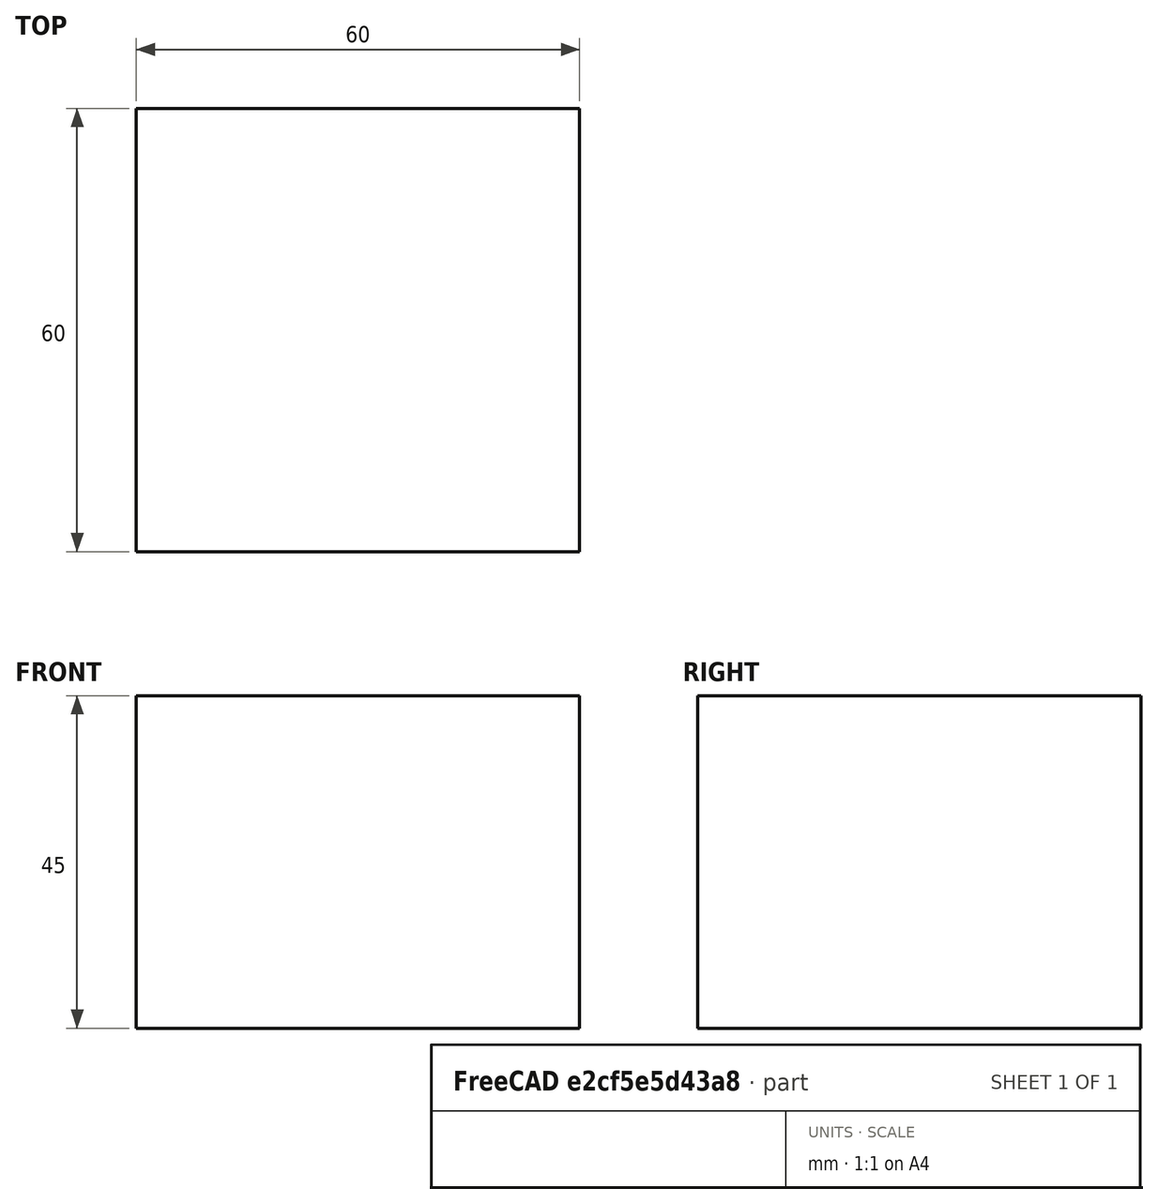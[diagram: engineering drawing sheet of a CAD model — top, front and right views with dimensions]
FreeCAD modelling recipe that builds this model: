
FCSTD DOCUMENT  (FreeCAD 0.15R4671 (Git))
Label: cad2
License: All rights reserved
LicenseURL: http://en.wikipedia.org/wiki/All_rights_reserved
objects: Part::Box×1, Sketcher::SketchObject×1
note: 2 computed .brp shape members not serialized (recipe doc carries the construction recipe); baked Part::Feature solids carry a one-line shape summary decoded from their .brp

FEATURE [Part::Box] Box  label="Cubo"
  Height = 45
  Length = 60
  Width = 60
FEATURE [Sketcher::SketchObject] Sketch
  Placement = pos=(0,0,45) rot=(0,0,1;0rad)
  sketch-geometry (27):
    g0: LineSegment StartX=5 StartY=55 StartZ=0 EndX=55 EndY=55 EndZ=0
    g1: LineSegment StartX=5 StartY=5 StartZ=0 EndX=55 EndY=5 EndZ=0
    g2: LineSegment StartX=5 StartY=55 StartZ=0 EndX=5 EndY=37.5 EndZ=0
    g3: LineSegment StartX=5 StartY=5 StartZ=0 EndX=5 EndY=22.5 EndZ=0
    g4: LineSegment StartX=5 StartY=22.5 StartZ=0 EndX=10 EndY=22.5 EndZ=0
    g5: LineSegment StartX=10 StartY=37.5 StartZ=0 EndX=5.0106 EndY=37.5 EndZ=0
    g6: LineSegment StartX=55 StartY=55 StartZ=0 EndX=55 EndY=37.5 EndZ=0
    g7: LineSegment StartX=55 StartY=5 StartZ=0 EndX=55 EndY=22.5 EndZ=0
    g8: LineSegment StartX=55 StartY=37.5 StartZ=0 EndX=50 EndY=37.5 EndZ=0
    g9: LineSegment StartX=50 StartY=22.5 StartZ=0 EndX=55 EndY=22.5 EndZ=0
    g10: GeomPoint [constr] X=60 Y=0 Z=0
    g11: GeomPoint [constr] X=60 Y=60 Z=0
    g12: GeomPoint [constr] X=0 Y=60 Z=0
    g13: LineSegment StartX=50.001 StartY=37.5 StartZ=0 EndX=45 EndY=37.5 EndZ=0
    g14: LineSegment StartX=45 StartY=37.5 StartZ=0 EndX=45 EndY=32.5 EndZ=0
    g15: LineSegment StartX=45 StartY=32.5 StartZ=0 EndX=50 EndY=32.5 EndZ=0
    g16: LineSegment StartX=50 StartY=27.5 StartZ=0 EndX=45 EndY=27.5 EndZ=0
    g17: LineSegment StartX=45 StartY=27.5 StartZ=0 EndX=45 EndY=22.5 EndZ=0
    g18: LineSegment StartX=45 StartY=22.5 StartZ=0 EndX=50.0094 EndY=22.4998 EndZ=0
    g19: LineSegment StartX=50 StartY=32.5 StartZ=0 EndX=50 EndY=27.5 EndZ=0
    g20: LineSegment StartX=10 StartY=37.5 StartZ=0 EndX=15 EndY=37.5 EndZ=0
    g21: LineSegment StartX=15 StartY=37.5 StartZ=0 EndX=15 EndY=32.5 EndZ=0
    g22: LineSegment StartX=15 StartY=32.5 StartZ=0 EndX=10 EndY=32.5 EndZ=0
    g23: LineSegment StartX=10 StartY=32.4939 StartZ=0 EndX=10 EndY=27.5 EndZ=0
    g24: LineSegment StartX=10 StartY=27.5 StartZ=0 EndX=15 EndY=27.5 EndZ=0
    g25: LineSegment StartX=15 StartY=27.5 StartZ=0 EndX=15 EndY=22.5 EndZ=0
    g26: LineSegment StartX=15 StartY=22.5 StartZ=0 EndX=10 EndY=22.5 EndZ=0
  constraints (80):
    c: DistanceY(g2,g0) = 17.5
    c: DistanceY(g5,g0) = 17.5
    c: DistanceX(g5,g2) = -5
    c: DistanceX(g4,g3) = -5
    c: DistanceY(g3,g1) = -17.5
    c: DistanceY(g2,g1) = -50
    c: DistanceY(g3,g0) = 50
    c: DistanceX(g1,g1) = 50
    c: DistanceY(g-1,g1) = 5
    c: DistanceX(g-1,g3) = 5
    c: DistanceY(g-1,g1) = 5
    c: DistanceY(g-1,g7) = 5
    c: DistanceY(g1,g0) = 50
    c: DistanceY(g1,g6) = 50
    c: DistanceX(g6,g8) = -5
    c: DistanceX(g9,g7) = 5
    c: DistanceY(g7,g1) = -17.5
    c: DistanceY(g8,g0) = 17.5
    c: DistanceX(g0,g0) = 50
    c: DistanceX(g1,g7) = 50
    c: DistanceX(g-1,g1) = 5
    c: DistanceX(g-1,g0) = 5
    c: DistanceX(g1,g10) = 5
    c: DistanceY(g1,g10) = -5
    c: DistanceX(g0,g11) = 5
    c: DistanceX(g6,g11) = 5
    c: DistanceY(g0,g11) = 5
    c: DistanceX(g8,g11) = 5
    c: DistanceX(g9,g11) = 10
    c: DistanceX(g9,g10) = 5
    c: DistanceX(g6,g11) = 5
    c: DistanceX(g8,g5) = -40
    c: DistanceX(g12,g2) = 5
    c: DistanceX(g12,g0) = 5
    c: DistanceY(g12,g0) = -5
    c: Coincident(g13,g14)
    c: Coincident(g14,g15)
    c: DistanceY(g13,g15) = -5
    c: DistanceY(g13,g14) = -5
    c: DistanceY(g8,g14) = -5
    c: DistanceY(g15,g8) = 5
    c: DistanceX(g6,g14) = -10
    c: Coincident(g16,g17)
    c: Coincident(g17,g18)
    c: DistanceX(g16,g16) = 5
    c: DistanceY(g16,g17) = -5
    c: DistanceY(g16,g9) = -5
    c: DistanceX(g15,g14) = -5
    c: DistanceX(g19,g16) = -5
    c: DistanceY(g19,g15) = 5
    c: DistanceY(g16,g15) = 5
    c: DistanceY(g19,g16) = -5
    c: DistanceY(g19,g16) = -5
    c: DistanceX(g16,g19) = 5
    c: DistanceX(g17,g7) = 10
    c: DistanceY(g7,g16) = 5
    c: Coincident(g20,g21)
    c: Coincident(g21,g22)
    c: Coincident(g23,g24)
    c: Coincident(g24,g25)
    c: Coincident(g25,g26)
    c: DistanceX(g25,g4) = -5
    c: DistanceX(g24,g23) = -5
    c: DistanceX(g26,g3) = -5
    c: DistanceY(g4,g24) = 5
    c: DistanceY(g26,g24) = 5
    c: DistanceY(g3,g24) = 5
    c: DistanceX(g4,g25) = 10
    c: DistanceY(g23,g25) = -5
    c: DistanceY(g23,g4) = -5
    c: DistanceX(g24,g4) = -5
    c: DistanceY(g24,g22) = 5
    c: DistanceX(g22,g24) = 5
    c: DistanceX(g23,g21) = 5
    c: DistanceY(g23,g21) = 5
    c: DistanceX(g21,g23) = -5
    c: DistanceY(g21,g20) = 5
    c: DistanceX(g22,g20) = 5
    c: DistanceX(g20,g5) = -5
    c: DistanceY(g20,g0) = 17.5
